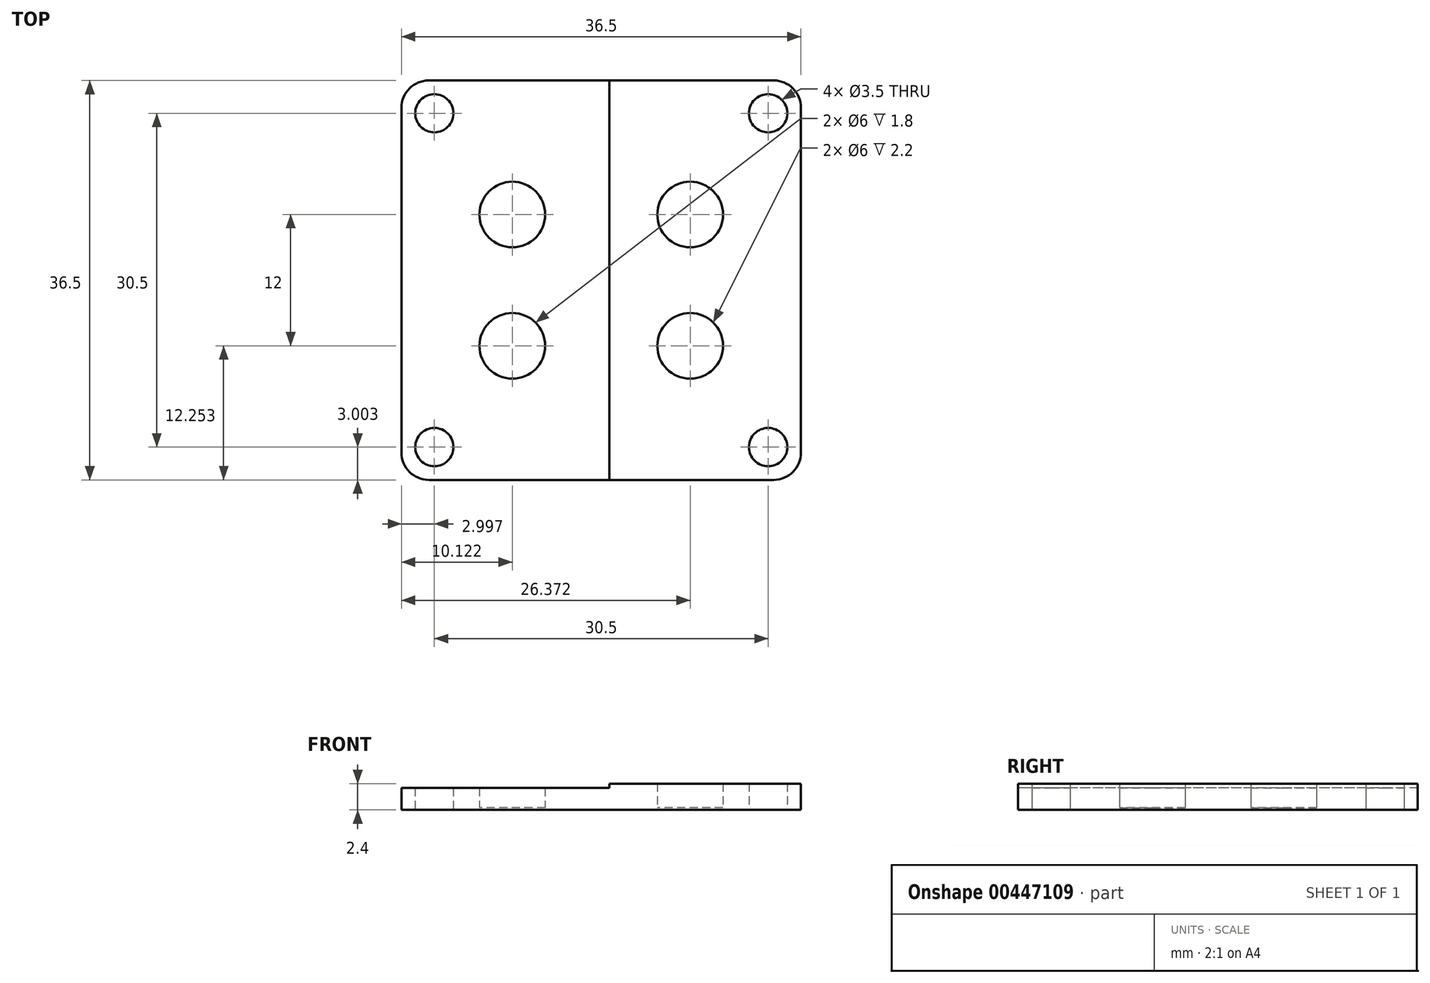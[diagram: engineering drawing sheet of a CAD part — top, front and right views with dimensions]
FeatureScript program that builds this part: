
annotation { "Feature Type Name" : "Feature", "Feature Type Description" : "" }
export const myFeature = defineFeature(function(context is Context, id is Id, definition is map)
    precondition{}
    {
        {
            var Q0;
            Q0=qCreatedBy(makeId("Top.planeOp"),FACE);
            var sketch = newSketch(context, id + "F0", { "sketchPlane" : qUnion([Q0])});
            skCircle(sketch, "E0", {"center": v(-32.98, 0.42) * mm, "radius": 1.75 * mm});
            skCircle(sketch, "E1", {"center": v(-2.48, 0.42) * mm, "radius": 1.75 * mm});
            skCircle(sketch, "E2", {"center": v(-2.48, -30.08) * mm, "radius": 1.75 * mm});
            skCircle(sketch, "E3", {"center": v(-32.98, -30.08) * mm, "radius": 1.75 * mm});
            skLineSegment(sketch, "E4.bottom", {"start": v(-35.98, 3.42) * mm, "end": v(0.52, 3.42) * mm});
            skLineSegment(sketch, "E4.top", {"start": v(-35.98, -33.08) * mm, "end": v(0.52, -33.08) * mm});
            skLineSegment(sketch, "E4.left", {"start": v(-35.98, 3.42) * mm, "end": v(-35.98, -33.08) * mm});
            skLineSegment(sketch, "E4.right", {"start": v(0.52, 3.42) * mm, "end": v(0.52, -33.08) * mm});
            skSolve(sketch);
        }
        {
            var Q0;
            Q0=makeQuery(id+"F0.imprint","IMPRINT",FACE,{"disambiguationData":[TD([[makeQuery(id+"F0.imprint","IMPRINT",EDGE,{"derivedFrom":sQuery(id+"F0.wireOp",EDGE,"E0")}),-1.0]])]});
            extrude(context, id + "F1", {"entities" : qUnion([Q0]), "depth" : .2 * mm});
        }
        {
            var Q0;
            Q0=makeQuery(id+"F1.opExtrude","CAP_FACE",FACE,{"disambiguationData":[OSD([sQuery(id+"F0.wireOp",EDGE,"E0"),sQuery(id+"F0.wireOp",EDGE,"E1"),sQuery(id+"F0.wireOp",EDGE,"E2"),sQuery(id+"F0.wireOp",EDGE,"E3"),sQuery(id+"F0.wireOp",EDGE,"E4.bottom"),sQuery(id+"F0.wireOp",EDGE,"E4.top"),sQuery(id+"F0.wireOp",EDGE,"E4.left"),sQuery(id+"F0.wireOp",EDGE,"E4.right")])],"isStart":false});
            var sketch = newSketch(context, id + "F2", { "sketchPlane" : qUnion([Q0])});
            skCircle(sketch, "E5", {"center": v(-25.86, -20.83) * mm, "radius": 3 * mm});
            skCircle(sketch, "E6", {"center": v(-9.6, -20.83) * mm, "radius": 3 * mm});
            skCircle(sketch, "E7", {"center": v(-9.6, -8.83) * mm, "radius": 3 * mm});
            skCircle(sketch, "E8", {"center": v(-25.86, -8.83) * mm, "radius": 3 * mm});
            skLineSegment(sketch, "E9", {"start": v(-32.98, 0.42) * mm, "end": v(-17.73, -14.83) * mm, "construction": true});
            skLineSegment(sketch, "E10", {"start": v(-17.73, -14.83) * mm, "end": v(-32.98, -30.08) * mm, "construction": true});
            skLineSegment(sketch, "E11", {"start": v(-25.86, -8.83) * mm, "end": v(-17.73, -14.83) * mm, "construction": true});
            skLineSegment(sketch, "E12", {"start": v(-9.6, -8.83) * mm, "end": v(-12.02, -10.6) * mm, "construction": true});
            skLineSegment(sketch, "E13.trimOffspring", {"start": v(-17.73, -14.83) * mm, "end": v(-25.86, -20.83) * mm, "construction": true});
            skLineSegment(sketch, "E14.trimOffspring", {"start": v(-12.02, -19.04) * mm, "end": v(-9.6, -20.83) * mm, "construction": true});
            skPoint(sketch, "E15.orphan", {"position": v(-2.48, 0.42) * mm});
            skPoint(sketch, "E16.orphan", {"position": v(-2.48, -30.08) * mm});
            skSolve(sketch);
        }
        {
            var Q0;
            Q0=makeQuery(id+"F2.imprint","IMPRINT",FACE,{"disambiguationData":[TD([[makeQuery(id+"F2.imprint","IMPRINT",EDGE,{"derivedFrom":sQuery(id+"F2.wireOp",EDGE,"E5")}),-1.0]])]});
            extrude(context, id + "F3", {"entities" : qUnion([Q0]), "operationType" : NewBodyOperationType.ADD, "depth" : 1.8 * mm});
        }
        {
            var Q0;
            Q0=makeQuery(id+"F3.opExtrude","CAP_FACE",FACE,{"disambiguationData":[OSD([sQuery(id+"F0.wireOp",EDGE,"E0"),sQuery(id+"F0.wireOp",EDGE,"E1"),sQuery(id+"F0.wireOp",EDGE,"E2"),sQuery(id+"F0.wireOp",EDGE,"E3"),sQuery(id+"F0.wireOp",EDGE,"E4.bottom"),sQuery(id+"F0.wireOp",EDGE,"E4.top"),sQuery(id+"F0.wireOp",EDGE,"E4.left"),sQuery(id+"F0.wireOp",EDGE,"E4.right"),sQuery(id+"F2.wireOp",EDGE,"E5"),sQuery(id+"F2.wireOp",EDGE,"E6"),sQuery(id+"F2.wireOp",EDGE,"E7"),sQuery(id+"F2.wireOp",EDGE,"E8")])],"isStart":false});
            var sketch = newSketch(context, id + "F4", { "sketchPlane" : qUnion([Q0])});
            skLineSegment(sketch, "E17.0", {"start": v(-16.98, 3.42) * mm, "end": v(0.52, 3.42) * mm});
            skLineSegment(sketch, "E18.0", {"start": v(0.52, 3.42) * mm, "end": v(0.52, -33.08) * mm});
            skLineSegment(sketch, "E19.0", {"start": v(-16.98, -33.08) * mm, "end": v(0.52, -33.08) * mm});
            skLineSegment(sketch, "E20", {"start": v(-16.98, 3.42) * mm, "end": v(-16.98, -33.08) * mm});
            skPoint(sketch, "E21.orphan", {"position": v(-35.98, 3.42) * mm});
            skPoint(sketch, "E22.orphan", {"position": v(-35.98, -33.08) * mm});
            skSolve(sketch);
        }
        {
            var Q0;
            Q0=makeQuery(id+"F4.imprint","IMPRINT",FACE,{"disambiguationData":[TD([[makeQuery(id+"F4.imprint","IMPRINT",EDGE,{"derivedFrom":sQuery(id+"F4.wireOp",EDGE,"E17.0")}),-1.0]])]});
            extrude(context, id + "F5", {"entities" : qUnion([Q0]), "operationType" : NewBodyOperationType.ADD, "depth" : .4 * mm});
        }
        {
            var Q0;
            {var subQ0=sQuery(id+"F0.wireOp",EDGE,"E4.left");var subQ1=sQuery(id+"F0.wireOp",EDGE,"E4.bottom");Q0=makeQuery(id+"F3.boolean.opBoolean","MERGE",EDGE,{"derivedFrom":[makeQuery(id+"F1.opExtrude","SWEPT_EDGE",EDGE,{"disambiguationData":[OSD([subQ1,subQ0])]}),makeQuery(id+"F3.opExtrude","SWEPT_EDGE",EDGE,{"disambiguationData":[OSD([subQ1,subQ0])]})]});}
            var Q1;
            {var subQ0=sQuery(id+"F0.wireOp",EDGE,"E4.left");var subQ1=sQuery(id+"F0.wireOp",EDGE,"E4.top");Q1=makeQuery(id+"F3.boolean.opBoolean","MERGE",EDGE,{"derivedFrom":[makeQuery(id+"F1.opExtrude","SWEPT_EDGE",EDGE,{"disambiguationData":[OSD([subQ1,subQ0])]}),makeQuery(id+"F3.opExtrude","SWEPT_EDGE",EDGE,{"disambiguationData":[OSD([subQ1,subQ0])]})]});}
            var Q2;
            {var subQ0=sQuery(id+"F0.wireOp",EDGE,"E4.right");var subQ1=sQuery(id+"F0.wireOp",EDGE,"E4.top");Q2=makeQuery(id+"F3.boolean.opBoolean","MERGE",EDGE,{"derivedFrom":[makeQuery(id+"F1.opExtrude","SWEPT_EDGE",EDGE,{"disambiguationData":[OSD([subQ1,subQ0])]}),makeQuery(id+"F3.opExtrude","SWEPT_EDGE",EDGE,{"disambiguationData":[OSD([subQ1,subQ0])]})]});}
            var Q3;
            {var subQ0=sQuery(id+"F0.wireOp",EDGE,"E4.right");var subQ1=sQuery(id+"F0.wireOp",EDGE,"E4.bottom");Q3=makeQuery(id+"F3.boolean.opBoolean","MERGE",EDGE,{"derivedFrom":[makeQuery(id+"F1.opExtrude","SWEPT_EDGE",EDGE,{"disambiguationData":[OSD([subQ1,subQ0])]}),makeQuery(id+"F3.opExtrude","SWEPT_EDGE",EDGE,{"disambiguationData":[OSD([subQ1,subQ0])]})]});}
            fillet(context, id + "F6", {"entities" : qUnion([Q0, Q1, Q2, Q3]), "radius" : 2.5 * mm, "tangentPropagation" : true, "allowEdgeOverflow" : false});
        }
    });
